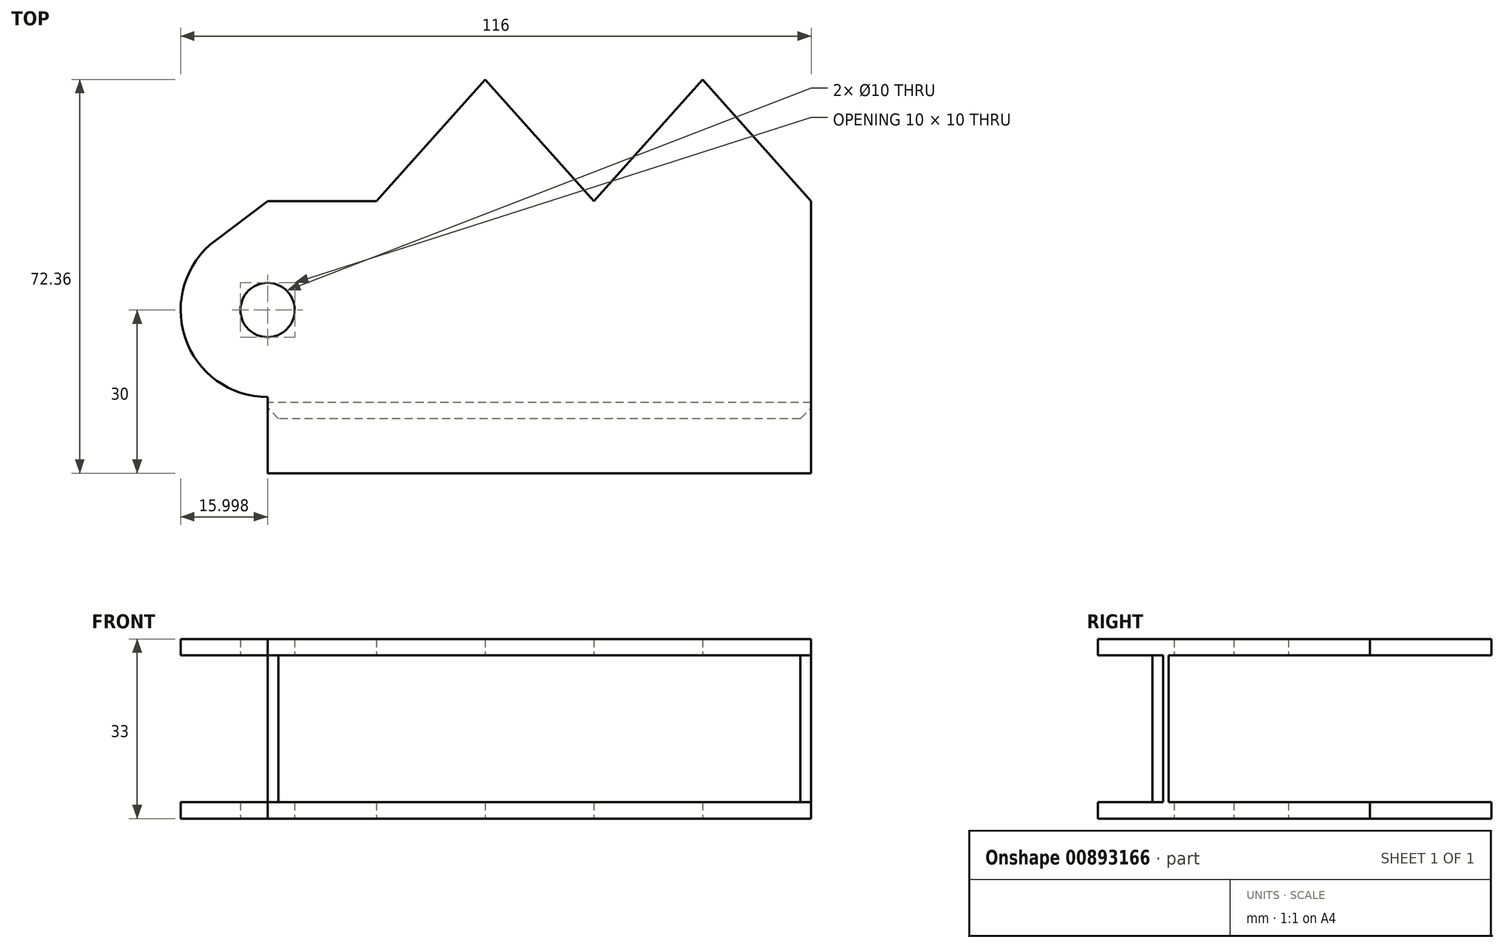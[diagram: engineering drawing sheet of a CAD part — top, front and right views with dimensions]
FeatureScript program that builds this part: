
annotation { "Feature Type Name" : "Feature", "Feature Type Description" : "" }
export const myFeature = defineFeature(function(context is Context, id is Id, definition is map)
    precondition{}
    {
        {
            var Q0;
            Q0=qCreatedBy(makeId("Top.planeOp"),FACE);
            var sketch = newSketch(context, id + "F0", { "sketchPlane" : qUnion([Q0])});
            skLineSegment(sketch, "E0", {"start": v(21.78, 56.67) * mm, "end": v(-78.22, 56.67) * mm});
            skLineSegment(sketch, "E1", {"start": v(-78.22, 56.67) * mm, "end": v(-78.22, 16.67) * mm});
            skPoint(sketch, "E2.startSnap0", {"position": v(41.78, 36.67) * mm});
            skCircle(sketch, "E3", {"center": v(21.78, 36.67) * mm, "radius": 5 * mm});
            skPoint(sketch, "E4.orphan", {"position": v(41.78, 56.67) * mm});
            skPoint(sketch, "E5.start.orphan", {"position": v(41.78, 16.67) * mm});
            skLineSegment(sketch, "E6", {"start": v(-18.22, -5.7) * mm, "end": v(-18.22, -7.75) * mm});
            skLineSegment(sketch, "E7", {"start": v(-38.22, 16.67) * mm, "end": v(-58.22, -5.7) * mm});
            skLineSegment(sketch, "E8", {"start": v(-58.22, -5.7) * mm, "end": v(-78.22, 16.67) * mm});
            skLineSegment(sketch, "E9", {"start": v(-38.22, 16.67) * mm, "end": v(-18.22, -5.7) * mm});
            skPoint(sketch, "E9.endSnap0", {"position": v(-18.22, -7.75) * mm});
            skLineSegment(sketch, "E10", {"start": v(-18.22, -5.7) * mm, "end": v(1.78, 16.67) * mm});
            skPoint(sketch, "E11.orphan", {"position": v(-18.22, -32.16) * mm});
            skLineSegment(sketch, "E12.trimOffspring", {"start": v(1.78, 16.67) * mm, "end": v(21.78, 16.67) * mm});
            skPoint(sketch, "E13.orphan", {"position": v(-18.22, 16.67) * mm});
            skArc(sketch, "E14", {"start": v(31.38, 23.87) * mm, "mid": v(36.96, 41.73) * mm, "end": v(21.78, 52.67) * mm});
            skLineSegment(sketch, "E15", {"start": v(21.78, 56.67) * mm, "end": v(21.78, 52.67) * mm});
            skLineSegment(sketch, "E16", {"start": v(21.78, 16.67) * mm, "end": v(31.38, 23.87) * mm});
            skSolve(sketch);
        }
        {
            var Q0;
            Q0=qSketchRegion(id+"F0",true);
            extrude(context, id + "F1", {"entities" : qUnion([Q0]), "depth" : 33 * mm, "offsetDistance" : 25 * mm});
        }
        {
            var Q0;
            Q0=makeQuery(id+"F1.opExtrude","SWEPT_BODY",BODY,{"disambiguationData":[OSD([sQuery(id+"F0.wireOp",EDGE,"E0"),sQuery(id+"F0.wireOp",EDGE,"E1"),sQuery(id+"F0.wireOp",EDGE,"538490fa-0efd-4a56-b3e3-c0d5682f8158"),sQuery(id+"F0.wireOp",EDGE,"E3"),sQuery(id+"F0.wireOp",EDGE,"E7"),sQuery(id+"F0.wireOp",EDGE,"E8"),sQuery(id+"F0.wireOp",EDGE,"E9"),sQuery(id+"F0.wireOp",EDGE,"E10"),sQuery(id+"F0.wireOp",EDGE,"E12.trimOffspring")])]});
            transform(context, id + "F2", {"entities" : qUnion([Q0]), "transformType" : TransformType.TRANSLATION_3D, "dx" : 0 * mm, "dy" : 0 * mm, "dz" : 28 * mm, "makeCopy" : true});
        }
        {
            var Q0;
            Q0=makeQuery(id+"F2.opPattern","COPY",BODY,{"derivedFrom":makeQuery(id+"F1.opExtrude","SWEPT_BODY",BODY,{"disambiguationData":[OSD([sQuery(id+"F0.wireOp",EDGE,"E0"),sQuery(id+"F0.wireOp",EDGE,"E1"),sQuery(id+"F0.wireOp",EDGE,"538490fa-0efd-4a56-b3e3-c0d5682f8158"),sQuery(id+"F0.wireOp",EDGE,"E3"),sQuery(id+"F0.wireOp",EDGE,"E7"),sQuery(id+"F0.wireOp",EDGE,"E8"),sQuery(id+"F0.wireOp",EDGE,"E9"),sQuery(id+"F0.wireOp",EDGE,"E10"),sQuery(id+"F0.wireOp",EDGE,"E12.trimOffspring")])]}),"instanceName":"1"});
            deleteBodies(context, id + "F3", {"entities" : qUnion([Q0])});
        }
        {
            var Q0;
            Q0=makeQuery(id+"F1.opExtrude","SWEPT_BODY",BODY,{"disambiguationData":[OSD([sQuery(id+"F0.wireOp",EDGE,"E0"),sQuery(id+"F0.wireOp",EDGE,"E1"),sQuery(id+"F0.wireOp",EDGE,"538490fa-0efd-4a56-b3e3-c0d5682f8158"),sQuery(id+"F0.wireOp",EDGE,"E3"),sQuery(id+"F0.wireOp",EDGE,"E7"),sQuery(id+"F0.wireOp",EDGE,"E8"),sQuery(id+"F0.wireOp",EDGE,"E9"),sQuery(id+"F0.wireOp",EDGE,"E10"),sQuery(id+"F0.wireOp",EDGE,"E12.trimOffspring")])]});
            transform(context, id + "F4", {"entities" : qUnion([Q0]), "transformType" : TransformType.TRANSLATION_3D, "dx" : 0 * mm, "dy" : 0 * mm, "dz" : 34 * mm, "makeCopy" : true});
        }
        {
            var Q0;
            Q0=makeQuery(id+"F1.opExtrude","CAP_FACE",FACE,{"disambiguationData":[OSD([sQuery(id+"F0.wireOp",EDGE,"E0"),sQuery(id+"F0.wireOp",EDGE,"E1"),sQuery(id+"F0.wireOp",EDGE,"538490fa-0efd-4a56-b3e3-c0d5682f8158"),sQuery(id+"F0.wireOp",EDGE,"E3"),sQuery(id+"F0.wireOp",EDGE,"E7"),sQuery(id+"F0.wireOp",EDGE,"E8"),sQuery(id+"F0.wireOp",EDGE,"E9"),sQuery(id+"F0.wireOp",EDGE,"E10"),sQuery(id+"F0.wireOp",EDGE,"E12.trimOffspring")])],"isStart":false});
            var sketch = newSketch(context, id + "F5", { "sketchPlane" : qUnion([Q0])});
            skLineSegment(sketch, "E17", {"start": v(-78.22, 56.67) * mm, "end": v(-78.22, 53.67) * mm});
            skLineSegment(sketch, "E18", {"start": v(-78.22, 53.67) * mm, "end": v(21.78, 53.67) * mm});
            skLineSegment(sketch, "E19", {"start": v(21.78, 53.67) * mm, "end": v(21.78, 56.67) * mm});
            skLineSegment(sketch, "E20", {"start": v(21.78, 56.67) * mm, "end": v(-78.22, 56.67) * mm});
            skSolve(sketch);
        }
        {
            var Q0;
            Q0=qSketchRegion(id+"F5",true);
            extrude(context, id + "F6", {"entities" : qUnion([Q0]), "depth" : 28 * mm, "offsetDistance" : 25 * mm});
        }
        {
            var Q0;
            Q0=makeQuery(id+"F6.opExtrude","SWEPT_FACE",FACE,{"disambiguationData":[OSD([sQuery(id+"F5.wireOp",EDGE,"E20")])]});
            var sketch = newSketch(context, id + "F7", { "sketchPlane" : qUnion([Q0])});
            skLineSegment(sketch, "E21", {"start": v(-21.78, 61) * mm, "end": v(-21.78, 64) * mm});
            skLineSegment(sketch, "E22", {"start": v(-21.78, 64) * mm, "end": v(78.22, 64) * mm});
            skLineSegment(sketch, "E23", {"start": v(78.22, 64) * mm, "end": v(78.22, 61) * mm});
            skLineSegment(sketch, "E24", {"start": v(78.22, 61) * mm, "end": v(-21.78, 61) * mm});
            skLineSegment(sketch, "E25", {"start": v(-21.78, 33) * mm, "end": v(78.22, 33) * mm});
            skLineSegment(sketch, "E26", {"start": v(78.22, 33) * mm, "end": v(78.22, 0) * mm});
            skLineSegment(sketch, "E27", {"start": v(78.22, 0) * mm, "end": v(-21.78, 0) * mm});
            skLineSegment(sketch, "E28", {"start": v(-21.78, 0) * mm, "end": v(-21.78, 33) * mm});
            skSolve(sketch);
        }
        {
            var Q0;
            Q0=qSketchRegion(id+"F7",true);
            extrude(context, id + "F8", {"entities" : qUnion([Q0]), "depth" : 10 * mm, "offsetDistance" : 25 * mm});
        }
        {
            var Q0;
            Q0=makeQuery(id+"F4.opPattern","COPY",BODY,{"derivedFrom":makeQuery(id+"F1.opExtrude","SWEPT_BODY",BODY,{"disambiguationData":[OSD([sQuery(id+"F0.wireOp",EDGE,"E0"),sQuery(id+"F0.wireOp",EDGE,"E1"),sQuery(id+"F0.wireOp",EDGE,"538490fa-0efd-4a56-b3e3-c0d5682f8158"),sQuery(id+"F0.wireOp",EDGE,"E3"),sQuery(id+"F0.wireOp",EDGE,"E7"),sQuery(id+"F0.wireOp",EDGE,"E8"),sQuery(id+"F0.wireOp",EDGE,"E9"),sQuery(id+"F0.wireOp",EDGE,"E10"),sQuery(id+"F0.wireOp",EDGE,"E12.trimOffspring")])]}),"instanceName":"1"});
            deleteBodies(context, id + "F9", {"entities" : qUnion([Q0])});
        }
        {
            var Q0;
            Q0=makeQuery(id+"F6.opExtrude","SWEPT_BODY",BODY,{"disambiguationData":[OSD([sQuery(id+"F5.wireOp",EDGE,"E17"),sQuery(id+"F5.wireOp",EDGE,"E18"),sQuery(id+"F5.wireOp",EDGE,"E19"),sQuery(id+"F5.wireOp",EDGE,"E20")])]});
            deleteBodies(context, id + "F10", {"entities" : qUnion([Q0])});
        }
        {
            var Q0;
            Q0=makeQuery(id+"F8.opExtrude","SWEPT_BODY",BODY,{"disambiguationData":[OSD([sQuery(id+"F7.wireOp",EDGE,"E21"),sQuery(id+"F7.wireOp",EDGE,"E22"),sQuery(id+"F7.wireOp",EDGE,"E23"),sQuery(id+"F7.wireOp",EDGE,"E24")])]});
            var Q1;
            Q1=makeQuery(id+"F8.opExtrude","SWEPT_BODY",BODY,{"disambiguationData":[OSD([sQuery(id+"F7.wireOp",EDGE,"E25"),sQuery(id+"F7.wireOp",EDGE,"E26"),sQuery(id+"F7.wireOp",EDGE,"E27"),sQuery(id+"F7.wireOp",EDGE,"E28")])]});
            deleteBodies(context, id + "F11", {"entities" : qUnion([Q0, Q1])});
        }
        {
            var Q0;
            Q0=makeQuery(id+"F1.opExtrude","SWEPT_FACE",FACE,{"disambiguationData":[OSD([sQuery(id+"F0.wireOp",EDGE,"E1")])]});
            var sketch = newSketch(context, id + "F12", { "sketchPlane" : qUnion([Q0])});
            skLineSegment(sketch, "E29", {"start": v(-53.67, 30) * mm, "end": v(15.53, 30) * mm});
            skLineSegment(sketch, "E30", {"start": v(-53.67, 3) * mm, "end": v(13.7, 3) * mm});
            skLineSegment(sketch, "E31", {"start": v(13.7, 3) * mm, "end": v(15.53, 30) * mm});
            skLineSegment(sketch, "E32", {"start": v(-53.67, 3) * mm, "end": v(-53.67, 30) * mm});
            skSolve(sketch);
        }
        {
            var Q0;
            Q0=qSketchRegion(id+"F12",true);
            extrude(context, id + "F13", {"entities" : qUnion([Q0]), "operationType" : NewBodyOperationType.REMOVE, "endBound" : BoundingType.THROUGH_ALL, "oppositeDirection" : true, "depth" : 25 * mm, "offsetDistance" : 25 * mm});
        }
        {
            var Q0;
            Q0=makeQuery(id+"F1.opExtrude","SWEPT_FACE",FACE,{"disambiguationData":[OSD([sQuery(id+"F0.wireOp",EDGE,"E0")])]});
            var sketch = newSketch(context, id + "F14", { "sketchPlane" : qUnion([Q0])});
            skLineSegment(sketch, "E33", {"start": v(-21.78, 0) * mm, "end": v(-21.78, 3) * mm});
            skLineSegment(sketch, "E34", {"start": v(-21.78, 3) * mm, "end": v(78.22, 3) * mm});
            skLineSegment(sketch, "E35", {"start": v(78.22, 3) * mm, "end": v(78.22, 0) * mm});
            skLineSegment(sketch, "E36", {"start": v(78.22, 0) * mm, "end": v(-21.78, 0) * mm});
            skLineSegment(sketch, "E37", {"start": v(-21.78, 33) * mm, "end": v(-21.78, 30) * mm});
            skLineSegment(sketch, "E38", {"start": v(-21.78, 30) * mm, "end": v(78.22, 30) * mm});
            skLineSegment(sketch, "E39", {"start": v(78.22, 30) * mm, "end": v(78.22, 33) * mm});
            skLineSegment(sketch, "E40", {"start": v(78.22, 33) * mm, "end": v(-21.78, 33) * mm});
            skSolve(sketch);
        }
        {
            var Q0;
            Q0=qSketchRegion(id+"F14",true);
            extrude(context, id + "F15", {"entities" : qUnion([Q0]), "operationType" : NewBodyOperationType.ADD, "depth" : 10 * mm, "offsetDistance" : 25 * mm});
        }
        {
            var Q0;
            Q0=makeQuery(id+"F1.opExtrude","SWEPT_BODY",BODY,{"disambiguationData":[OSD([sQuery(id+"F0.wireOp",EDGE,"E0"),sQuery(id+"F0.wireOp",EDGE,"E1"),sQuery(id+"F0.wireOp",EDGE,"E3"),sQuery(id+"F0.wireOp",EDGE,"E7"),sQuery(id+"F0.wireOp",EDGE,"E8"),sQuery(id+"F0.wireOp",EDGE,"E9"),sQuery(id+"F0.wireOp",EDGE,"E10"),sQuery(id+"F0.wireOp",EDGE,"E12.trimOffspring"),sQuery(id+"F0.wireOp",EDGE,"E14"),sQuery(id+"F0.wireOp",EDGE,"E15"),sQuery(id+"F0.wireOp",EDGE,"E16")])]});
            var Q1;
            Q1=makeQuery(id+"F15.boolean.opBoolean","MERGE",FACE,{"derivedFrom":[makeQuery(id+"F1.opExtrude","SWEPT_FACE",FACE,{"disambiguationData":[OSD([sQuery(id+"F0.wireOp",EDGE,"E1")])]}),makeQuery(id+"F15.opExtrude","SWEPT_FACE",FACE,{"disambiguationData":[OSD([sQuery(id+"F14.wireOp",EDGE,"E35")])]}),makeQuery(id+"F15.opExtrude","SWEPT_FACE",FACE,{"disambiguationData":[OSD([sQuery(id+"F14.wireOp",EDGE,"E39")])]})]});
            mirror(context, id + "F16", {"operationType" : NewBodyOperationType.ADD, "entities" : qUnion([Q0]), "mirrorPlane" : qUnion([Q1])});
        }
        {
            var Q0;
            {var subQ0=makeQuery(id+"F15.boolean.opBoolean","MERGE",FACE,{"derivedFrom":[makeQuery(id+"F1.opExtrude","CAP_FACE",FACE,{"disambiguationData":[OSD([sQuery(id+"F0.wireOp",EDGE,"E0"),sQuery(id+"F0.wireOp",EDGE,"E1"),sQuery(id+"F0.wireOp",EDGE,"E3"),sQuery(id+"F0.wireOp",EDGE,"E7"),sQuery(id+"F0.wireOp",EDGE,"E8"),sQuery(id+"F0.wireOp",EDGE,"E9"),sQuery(id+"F0.wireOp",EDGE,"E10"),sQuery(id+"F0.wireOp",EDGE,"E12.trimOffspring"),sQuery(id+"F0.wireOp",EDGE,"E14"),sQuery(id+"F0.wireOp",EDGE,"E15"),sQuery(id+"F0.wireOp",EDGE,"E16")])],"isStart":false}),makeQuery(id+"F15.opExtrude","SWEPT_FACE",FACE,{"disambiguationData":[OSD([sQuery(id+"F14.wireOp",EDGE,"E40")])]})]});Q0=makeQuery(id+"F16.boolean.opBoolean","MERGE",FACE,{"derivedFrom":[subQ0,makeQuery(id+"F16.opPattern","COPY",FACE,{"derivedFrom":subQ0,"instanceName":"1"})]});}
            var sketch = newSketch(context, id + "F17", { "sketchPlane" : qUnion([Q0])});
            skLineSegment(sketch, "E41", {"start": v(-78.22, 16.67) * mm, "end": v(-78.22, 86.7) * mm});
            skLineSegment(sketch, "E42", {"start": v(-78.22, 86.7) * mm, "end": v(68.21, 86.7) * mm});
            skLineSegment(sketch, "E43", {"start": v(68.21, 86.7) * mm, "end": v(68.21, -27.72) * mm});
            skLineSegment(sketch, "E44", {"start": v(68.21, -27.72) * mm, "end": v(-78.22, -27.72) * mm});
            skLineSegment(sketch, "E45", {"start": v(-78.22, -27.72) * mm, "end": v(-78.22, 16.67) * mm});
            skSolve(sketch);
        }
        {
            var Q0;
            Q0=qSketchRegion(id+"F17",true);
            extrude(context, id + "F18", {"entities" : qUnion([Q0]), "operationType" : NewBodyOperationType.REMOVE, "endBound" : BoundingType.THROUGH_ALL, "oppositeDirection" : true, "depth" : 25 * mm, "offsetDistance" : 25 * mm});
        }
        {
            var Q0;
            Q0=makeQuery(id+"F1.opExtrude","SWEPT_BODY",BODY,{"disambiguationData":[OSD([sQuery(id+"F0.wireOp",EDGE,"E0"),sQuery(id+"F0.wireOp",EDGE,"E1"),sQuery(id+"F0.wireOp",EDGE,"E3"),sQuery(id+"F0.wireOp",EDGE,"E7"),sQuery(id+"F0.wireOp",EDGE,"E8"),sQuery(id+"F0.wireOp",EDGE,"E9"),sQuery(id+"F0.wireOp",EDGE,"E10"),sQuery(id+"F0.wireOp",EDGE,"E12.trimOffspring"),sQuery(id+"F0.wireOp",EDGE,"E14"),sQuery(id+"F0.wireOp",EDGE,"E15"),sQuery(id+"F0.wireOp",EDGE,"E16")])]});
            var Q1;
            Q1=makeQuery(id+"F18.boolean.opBoolean","COPY",FACE,{"derivedFrom":makeQuery(id+"F18.opExtrude","SWEPT_FACE",FACE,{"disambiguationData":[OSD([sQuery(id+"F17.wireOp",EDGE,"E41"),sQuery(id+"F17.wireOp",EDGE,"E45")])]})});
            mirror(context, id + "F19", {"operationType" : NewBodyOperationType.ADD, "entities" : qUnion([Q0]), "mirrorPlane" : qUnion([Q1])});
        }
        {
            var Q0;
            {var subQ0=makeQuery(id+"F15.boolean.opBoolean","MERGE",FACE,{"derivedFrom":[makeQuery(id+"F1.opExtrude","CAP_FACE",FACE,{"disambiguationData":[OSD([sQuery(id+"F0.wireOp",EDGE,"E0"),sQuery(id+"F0.wireOp",EDGE,"E1"),sQuery(id+"F0.wireOp",EDGE,"E3"),sQuery(id+"F0.wireOp",EDGE,"E7"),sQuery(id+"F0.wireOp",EDGE,"E8"),sQuery(id+"F0.wireOp",EDGE,"E9"),sQuery(id+"F0.wireOp",EDGE,"E10"),sQuery(id+"F0.wireOp",EDGE,"E12.trimOffspring"),sQuery(id+"F0.wireOp",EDGE,"E14"),sQuery(id+"F0.wireOp",EDGE,"E15"),sQuery(id+"F0.wireOp",EDGE,"E16")])],"isStart":false}),makeQuery(id+"F15.opExtrude","SWEPT_FACE",FACE,{"disambiguationData":[OSD([sQuery(id+"F14.wireOp",EDGE,"E40")])]})]});var subQ1=makeQuery(id+"F16.boolean.opBoolean","MERGE",FACE,{"derivedFrom":[subQ0,makeQuery(id+"F16.opPattern","COPY",FACE,{"derivedFrom":subQ0,"instanceName":"1"})]});Q0=makeQuery(id+"F19.boolean.opBoolean","MERGE",FACE,{"derivedFrom":[subQ1,makeQuery(id+"F19.opPattern","COPY",FACE,{"derivedFrom":subQ1,"instanceName":"1"})]});}
            var sketch = newSketch(context, id + "F20", { "sketchPlane" : qUnion([Q0])});
            skLineSegment(sketch, "E46", {"start": v(-78.22, 66.67) * mm, "end": v(-78.22, -28.4) * mm});
            skLineSegment(sketch, "E47", {"start": v(-78.22, -28.4) * mm, "end": v(54.23, -31.85) * mm});
            skLineSegment(sketch, "E48", {"start": v(54.23, -31.85) * mm, "end": v(54.23, 66.67) * mm});
            skLineSegment(sketch, "E49", {"start": v(54.23, 66.67) * mm, "end": v(-78.22, 66.67) * mm});
            skSolve(sketch);
        }
        {
            var Q0;
            Q0 = qSketchRegion(id + "F20", true);
            extrude(context, id + "F21", {"entities" : qUnion([Q0]), "operationType" : NewBodyOperationType.REMOVE, "endBound" : BoundingType.THROUGH_ALL, "oppositeDirection" : true, "depth" : 25 * mm, "offsetDistance" : 25 * mm});
        }
        {
            var Q0;
            Q0=makeQuery(id+"F1.opExtrude","SWEPT_BODY",BODY,{"disambiguationData":[OSD([sQuery(id+"F0.wireOp",EDGE,"E0"),sQuery(id+"F0.wireOp",EDGE,"E1"),sQuery(id+"F0.wireOp",EDGE,"E3"),sQuery(id+"F0.wireOp",EDGE,"E7"),sQuery(id+"F0.wireOp",EDGE,"E8"),sQuery(id+"F0.wireOp",EDGE,"E9"),sQuery(id+"F0.wireOp",EDGE,"E10"),sQuery(id+"F0.wireOp",EDGE,"E12.trimOffspring"),sQuery(id+"F0.wireOp",EDGE,"E14"),sQuery(id+"F0.wireOp",EDGE,"E15"),sQuery(id+"F0.wireOp",EDGE,"E16")])]});
            var Q1;
            {var subQ0=makeQuery(id+"F15.opExtrude","CAP_FACE",FACE,{"disambiguationData":[OSD([sQuery(id+"F14.wireOp",EDGE,"E37"),sQuery(id+"F14.wireOp",EDGE,"E38"),sQuery(id+"F14.wireOp",EDGE,"E39"),sQuery(id+"F14.wireOp",EDGE,"E40")])],"isStart":false});var subQ1=makeQuery(id+"F16.boolean.opBoolean","MERGE",FACE,{"derivedFrom":[subQ0,makeQuery(id+"F16.opPattern","COPY",FACE,{"derivedFrom":subQ0,"instanceName":"1"})]});Q1=makeQuery(id+"F19.boolean.opBoolean","MERGE",FACE,{"derivedFrom":[subQ1,makeQuery(id+"F19.opPattern","COPY",FACE,{"derivedFrom":subQ1,"instanceName":"1"})]});}
            mirror(context, id + "F22", {"operationType" : NewBodyOperationType.ADD, "entities" : qUnion([Q0]), "mirrorPlane" : qUnion([Q1])});
        }
        {
            var Q0;
            {var subQ0=makeQuery(id+"F15.boolean.opBoolean","MERGE",FACE,{"derivedFrom":[makeQuery(id+"F1.opExtrude","CAP_FACE",FACE,{"disambiguationData":[OSD([sQuery(id+"F0.wireOp",EDGE,"E0"),sQuery(id+"F0.wireOp",EDGE,"E1"),sQuery(id+"F0.wireOp",EDGE,"E3"),sQuery(id+"F0.wireOp",EDGE,"E7"),sQuery(id+"F0.wireOp",EDGE,"E8"),sQuery(id+"F0.wireOp",EDGE,"E9"),sQuery(id+"F0.wireOp",EDGE,"E10"),sQuery(id+"F0.wireOp",EDGE,"E12.trimOffspring"),sQuery(id+"F0.wireOp",EDGE,"E14"),sQuery(id+"F0.wireOp",EDGE,"E15"),sQuery(id+"F0.wireOp",EDGE,"E16")])],"isStart":false}),makeQuery(id+"F15.opExtrude","SWEPT_FACE",FACE,{"disambiguationData":[OSD([sQuery(id+"F14.wireOp",EDGE,"E40")])]})]});var subQ1=makeQuery(id+"F16.boolean.opBoolean","MERGE",FACE,{"derivedFrom":[subQ0,makeQuery(id+"F16.opPattern","COPY",FACE,{"derivedFrom":subQ0,"instanceName":"1"})]});var subQ2=makeQuery(id+"F19.boolean.opBoolean","MERGE",FACE,{"derivedFrom":[subQ1,makeQuery(id+"F19.opPattern","COPY",FACE,{"derivedFrom":subQ1,"instanceName":"1"})]});Q0=makeQuery(id+"F22.boolean.opBoolean","MERGE",FACE,{"derivedFrom":[subQ2,makeQuery(id+"F22.opPattern","COPY",FACE,{"derivedFrom":subQ2,"instanceName":"1"})]});}
            var sketch = newSketch(context, id + "F23", { "sketchPlane" : qUnion([Q0])});
            skLineSegment(sketch, "E50", {"start": v(-78.22, 66.67) * mm, "end": v(-239.66, 66.67) * mm});
            skLineSegment(sketch, "E51", {"start": v(-239.66, 66.67) * mm, "end": v(-202.16, -18.21) * mm});
            skLineSegment(sketch, "E52", {"start": v(-202.16, -18.21) * mm, "end": v(-78.22, -18.21) * mm});
            skLineSegment(sketch, "E53", {"start": v(-78.22, -18.21) * mm, "end": v(-78.22, 66.67) * mm});
            skSolve(sketch);
        }
        {
            var Q0;
            Q0 = qSketchRegion(id + "F23", true);
            extrude(context, id + "F24", {"entities" : qUnion([Q0]), "operationType" : NewBodyOperationType.REMOVE, "endBound" : BoundingType.THROUGH_ALL, "oppositeDirection" : true, "depth" : 25 * mm, "offsetDistance" : 25 * mm});
        }
        {
            var Q0;
            Q0=makeQuery(id+"F22.opPattern","COPY",EDGE,{"derivedFrom":makeQuery(id+"F16.opPattern","COPY",EDGE,{"derivedFrom":makeQuery(id+"F1.opExtrude","SWEPT_EDGE",EDGE,{"disambiguationData":[OSD([sQuery(id+"F0.wireOp",EDGE,"E0"),sQuery(id+"F0.wireOp",EDGE,"E15")])]}),"instanceName":"1"}),"instanceName":"1"});
            var Q1;
            {var subQ0=makeQuery(id+"F1.opExtrude","SWEPT_FACE",FACE,{"disambiguationData":[OSD([sQuery(id+"F0.wireOp",EDGE,"E0")])]});var subQ1=makeQuery(id+"F16.boolean.opBoolean","MERGE",FACE,{"derivedFrom":[subQ0,makeQuery(id+"F16.opPattern","COPY",FACE,{"derivedFrom":subQ0,"instanceName":"1"})]});Q1=makeQuery(id+"F22.opPattern","COPY",EDGE,{"derivedFrom":makeQuery(id+"F21.boolean.opBoolean","INTERSECT",EDGE,{"derivedFrom":[makeQuery(id+"F19.boolean.opBoolean","MERGE",FACE,{"derivedFrom":[subQ1,makeQuery(id+"F19.opPattern","COPY",FACE,{"derivedFrom":subQ1,"instanceName":"1"})]}),makeQuery(id+"F21.opExtrude","SWEPT_FACE",FACE,{"disambiguationData":[OSD([sQuery(id+"F20.wireOp",EDGE,"E46")])]})]}),"instanceName":"1"});}
            chamfer(context, id + "F25", {"entities" : qUnion([Q0, Q1]), "width" : 2 * mm, "tangentPropagation" : true});
        }
    });
